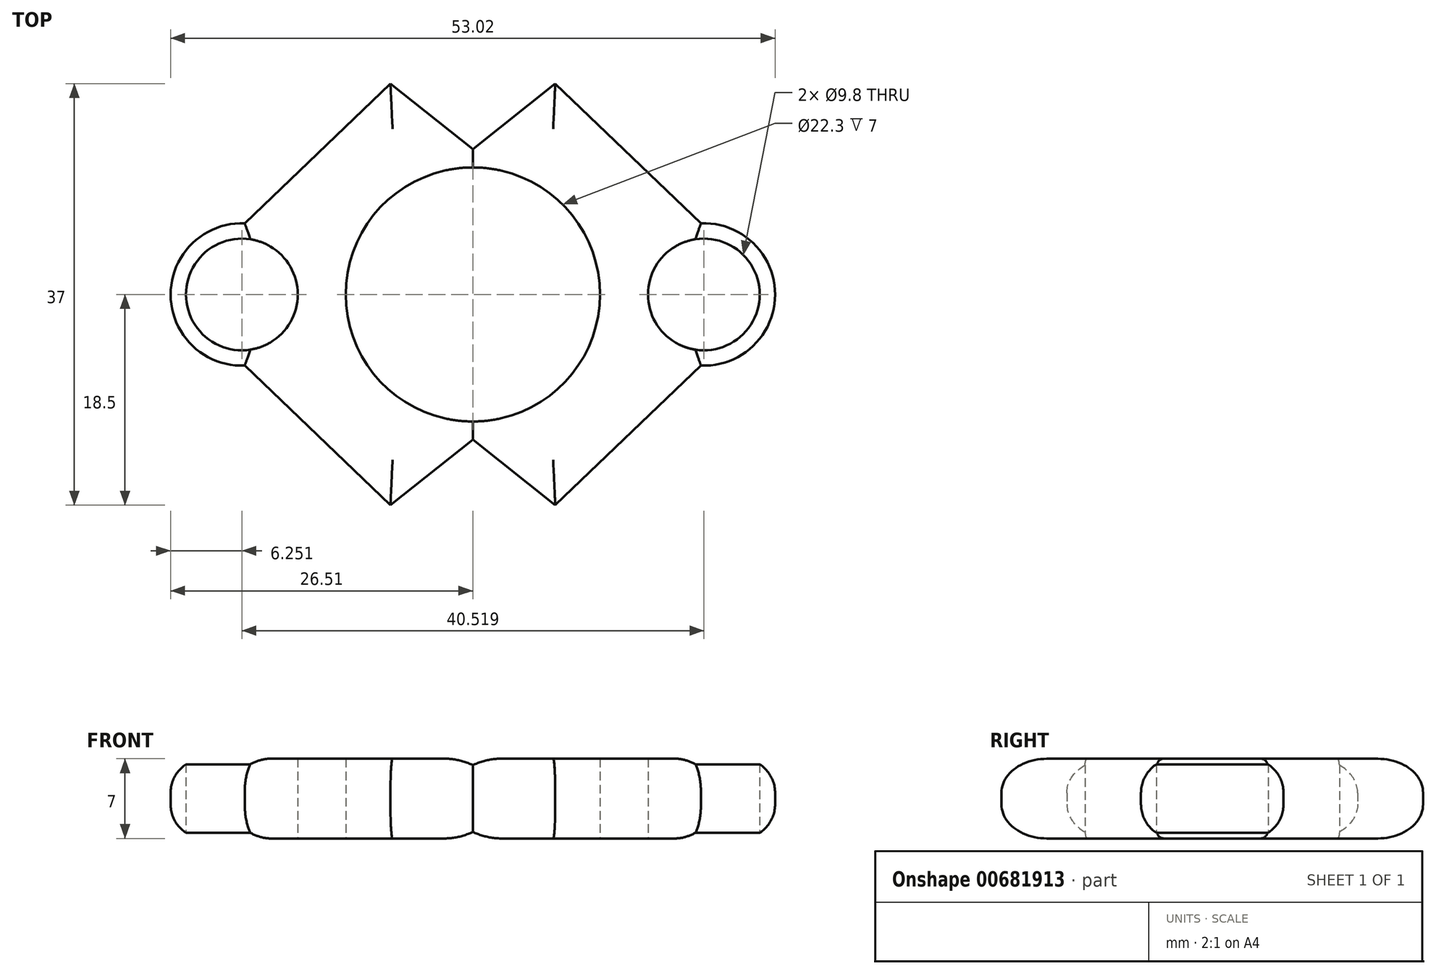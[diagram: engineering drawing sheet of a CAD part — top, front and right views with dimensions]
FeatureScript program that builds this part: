
annotation { "Feature Type Name" : "Feature", "Feature Type Description" : "" }
export const myFeature = defineFeature(function(context is Context, id is Id, definition is map)
    precondition{}
    {
        {
            var Q0;
            Q0=qCreatedBy(makeId("Top.planeOp"),FACE);
            var sketch = newSketch(context, id + "F0", { "sketchPlane" : qUnion([Q0])});
            skCircle(sketch, "E0", {"center": v(0, 0) * mm, "radius": 11.15 * mm});
            skCircle(sketch, "E1", {"center": v(0, 0) * mm, "radius": 12.75 * mm});
            skCircle(sketch, "E2", {"center": v(-20.26, 0) * mm, "radius": 4.9 * mm});
            skLineSegment(sketch, "E3", {"start": v(-21.61, 4.7) * mm, "end": v(-7.23, 18.5) * mm});
            skLineSegment(sketch, "E4", {"start": v(-7.23, 18.5) * mm, "end": v(0, 12.75) * mm});
            skLineSegment(sketch, "E5.MirrorCS", {"start": v(-7.23, -18.5) * mm, "end": v(0, -12.75) * mm});
            skLineSegment(sketch, "E6.MirrorCS", {"start": v(-21.61, -4.7) * mm, "end": v(-7.23, -18.5) * mm});
            skLineSegment(sketch, "E7.MirrorCS", {"start": v(21.61, -4.7) * mm, "end": v(7.23, -18.5) * mm});
            skLineSegment(sketch, "E8.MirrorCS", {"start": v(21.61, 4.7) * mm, "end": v(7.23, 18.5) * mm});
            skLineSegment(sketch, "E9.MirrorCS", {"start": v(7.23, -18.5) * mm, "end": v(0, -12.75) * mm});
            skLineSegment(sketch, "E10.MirrorCS", {"start": v(7.23, 18.5) * mm, "end": v(0, 12.75) * mm});
            skCircle(sketch, "E11.MirrorC", {"center": v(20.26, 0) * mm, "radius": 4.9 * mm});
            skCircle(sketch, "E12", {"center": v(-20.26, 0) * mm, "radius": 6.25 * mm});
            skCircle(sketch, "E13.MirrorC", {"center": v(20.26, 0) * mm, "radius": 6.25 * mm});
            skSolve(sketch);
        }
        {
            var Q0;
            Q0 = qSketchRegion(id + "F0", true);
            extrude(context, id + "F1", {"entities" : qUnion([Q0]), "depth" : 7 * mm, "offsetDistance" : 25 * mm});
        }
        {
            var Q0;
            Q0=makeQuery(id+"F1.opExtrude","CAP_EDGE",EDGE,{"disambiguationData":[OSD([sQuery(id+"F0.wireOp",EDGE,"E10.MirrorCS")])],"isStart":true});
            var Q1;
            Q1=makeQuery(id+"F1.opExtrude","CAP_EDGE",EDGE,{"disambiguationData":[OSD([sQuery(id+"F0.wireOp",EDGE,"E4")])],"isStart":true});
            var Q2;
            Q2=makeQuery(id+"F1.opExtrude","CAP_EDGE",EDGE,{"disambiguationData":[OSD([sQuery(id+"F0.wireOp",EDGE,"E3")])],"isStart":true});
            var Q3;
            Q3=makeQuery(id+"F1.opExtrude","CAP_EDGE",EDGE,{"disambiguationData":[OSD([sQuery(id+"F0.wireOp",EDGE,"E12")])],"isStart":true});
            var Q4;
            Q4=makeQuery(id+"F1.opExtrude","CAP_EDGE",EDGE,{"disambiguationData":[OSD([sQuery(id+"F0.wireOp",EDGE,"E6.MirrorCS")])],"isStart":true});
            var Q5;
            Q5=makeQuery(id+"F1.opExtrude","CAP_EDGE",EDGE,{"disambiguationData":[OSD([sQuery(id+"F0.wireOp",EDGE,"E5.MirrorCS")])],"isStart":true});
            var Q6;
            Q6=makeQuery(id+"F1.opExtrude","CAP_EDGE",EDGE,{"disambiguationData":[OSD([sQuery(id+"F0.wireOp",EDGE,"E9.MirrorCS")])],"isStart":true});
            var Q7;
            Q7=makeQuery(id+"F1.opExtrude","CAP_EDGE",EDGE,{"disambiguationData":[OSD([sQuery(id+"F0.wireOp",EDGE,"E3")])],"isStart":false});
            var Q8;
            Q8=makeQuery(id+"F1.opExtrude","CAP_EDGE",EDGE,{"disambiguationData":[OSD([sQuery(id+"F0.wireOp",EDGE,"E4")])],"isStart":false});
            var Q9;
            Q9=makeQuery(id+"F1.opExtrude","CAP_EDGE",EDGE,{"disambiguationData":[OSD([sQuery(id+"F0.wireOp",EDGE,"E10.MirrorCS")])],"isStart":false});
            var Q10;
            Q10=makeQuery(id+"F1.opExtrude","CAP_EDGE",EDGE,{"disambiguationData":[OSD([sQuery(id+"F0.wireOp",EDGE,"E8.MirrorCS")])],"isStart":false});
            var Q11;
            Q11=makeQuery(id+"F1.opExtrude","CAP_EDGE",EDGE,{"disambiguationData":[OSD([sQuery(id+"F0.wireOp",EDGE,"E12")])],"isStart":false});
            var Q12;
            Q12=makeQuery(id+"F1.opExtrude","CAP_EDGE",EDGE,{"disambiguationData":[OSD([sQuery(id+"F0.wireOp",EDGE,"E6.MirrorCS")])],"isStart":false});
            var Q13;
            Q13=makeQuery(id+"F1.opExtrude","CAP_EDGE",EDGE,{"disambiguationData":[OSD([sQuery(id+"F0.wireOp",EDGE,"E5.MirrorCS")])],"isStart":false});
            var Q14;
            Q14=makeQuery(id+"F1.opExtrude","CAP_EDGE",EDGE,{"disambiguationData":[OSD([sQuery(id+"F0.wireOp",EDGE,"E9.MirrorCS")])],"isStart":false});
            var Q15;
            Q15=makeQuery(id+"F1.opExtrude","CAP_EDGE",EDGE,{"disambiguationData":[OSD([sQuery(id+"F0.wireOp",EDGE,"E7.MirrorCS")])],"isStart":false});
            var Q16;
            Q16=makeQuery(id+"F1.opExtrude","CAP_EDGE",EDGE,{"disambiguationData":[OSD([sQuery(id+"F0.wireOp",EDGE,"E13.MirrorC")])],"isStart":false});
            var Q17;
            Q17=makeQuery(id+"F1.opExtrude","CAP_EDGE",EDGE,{"disambiguationData":[OSD([sQuery(id+"F0.wireOp",EDGE,"E13.MirrorC")])],"isStart":true});
            var Q18;
            Q18=makeQuery(id+"F1.opExtrude","CAP_EDGE",EDGE,{"disambiguationData":[OSD([sQuery(id+"F0.wireOp",EDGE,"E8.MirrorCS")])],"isStart":true});
            var Q19;
            Q19=makeQuery(id+"F1.opExtrude","CAP_EDGE",EDGE,{"disambiguationData":[OSD([sQuery(id+"F0.wireOp",EDGE,"E7.MirrorCS")])],"isStart":true});
            fillet(context, id + "F2", {"entities" : qUnion([Q0, Q1, Q2, Q3, Q4, Q5, Q6, Q7, Q8, Q9, Q10, Q11, Q12, Q13, Q14, Q15, Q16, Q17, Q18, Q19]), "radius" : 3 * mm, "tangentPropagation" : true, "allowEdgeOverflow" : false});
        }
    });
